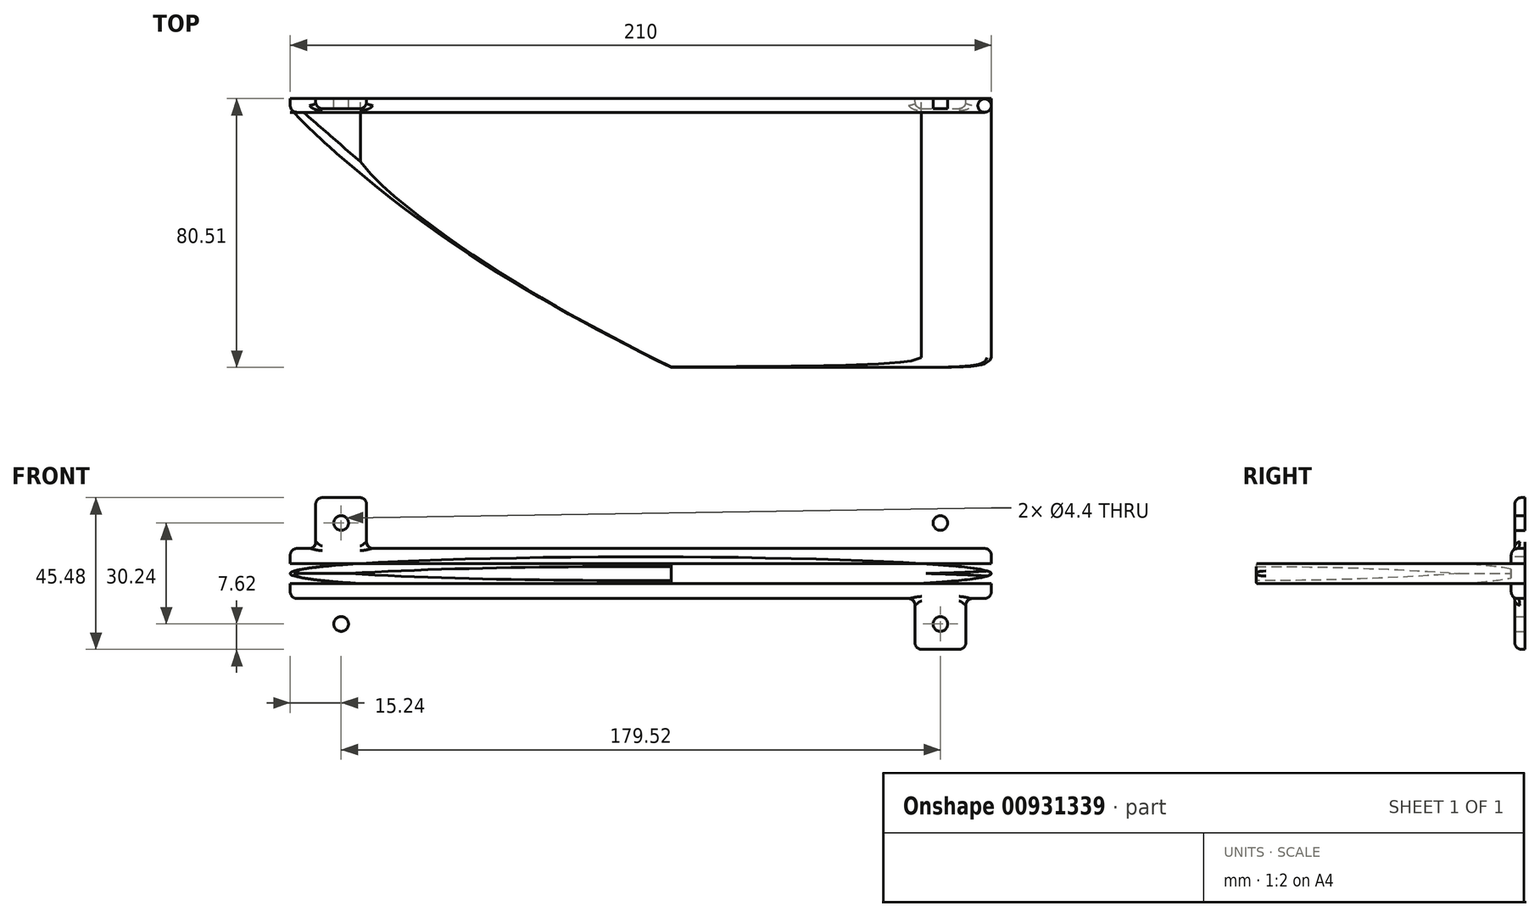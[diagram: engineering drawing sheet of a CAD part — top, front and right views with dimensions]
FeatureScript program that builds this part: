
annotation { "Feature Type Name" : "Feature", "Feature Type Description" : "" }
export const myFeature = defineFeature(function(context is Context, id is Id, definition is map)
    precondition{}
    {
        {
            var Q0;
            Q0=qCreatedBy(makeId("Top.planeOp"),FACE);
            var sketch = newSketch(context, id + "F0", { "sketchPlane" : qUnion([Q0])});
            skLineSegment(sketch, "E0", {"start": v(0, 0) * mm, "end": v(-180, 0) * mm});
            skLineSegment(sketch, "E1", {"start": v(0, 0) * mm, "end": v(30, 0) * mm});
            skLineSegment(sketch, "E2", {"start": v(30, 0) * mm, "end": v(30, -70) * mm});
            skFitSpline(sketch, "E3", {"points": [v(-180, 0) * mm, v(30, -70) * mm, v(30, 0) * mm], "startDerivative": vector(383.5, -279.58) * mm, "endDerivative": vector(-59.05, 249.16) * mm});
            skLineSegment(sketch, "E4.bottom", {"start": v(-180, 0) * mm, "end": v(50.04, 0) * mm});
            skLineSegment(sketch, "E5", {"start": v(3.9, -76.51) * mm, "end": v(3.9, 0) * mm});
            skLineSegment(sketch, "E6.bottom", {"start": v(-341.07, -177.66) * mm, "end": v(204.1, -177.66) * mm});
            skLineSegment(sketch, "E6.top", {"start": v(-341.07, 125.69) * mm, "end": v(204.1, 125.69) * mm});
            skLineSegment(sketch, "E6.left", {"start": v(-341.07, -177.66) * mm, "end": v(-341.07, 125.69) * mm});
            skLineSegment(sketch, "E6.right", {"start": v(204.1, -177.66) * mm, "end": v(204.1, 125.69) * mm});
            skPoint(sketch, "E6.middle", {"position": v(-68.48, -25.98) * mm});
            skSolve(sketch);
        }
        {
            var Q0;
            Q0=qCreatedBy(makeId("Front.planeOp"),FACE);
            var sketch = newSketch(context, id + "F1", { "sketchPlane" : qUnion([Q0])});
            skPoint(sketch, "E7", {"position": v(-75, 0) * mm});
            skLineSegment(sketch, "E8.1", {"start": v(0, 0) * mm, "end": v(30, 0) * mm});
            skEllipse(sketch, "E9", {"center": v(-75, 0) * mm, "majorRadius": 105 * mm, "minorRadius": 5 * mm, "majorAxis": v(-1, 0)});
            skLineSegment(sketch, "E10.bottom", {"start": v(-180, 3) * mm, "end": v(30, 3) * mm});
            skLineSegment(sketch, "E10.top", {"start": v(-180, -3) * mm, "end": v(30, -3) * mm});
            skLineSegment(sketch, "E10.left", {"start": v(-180, 3) * mm, "end": v(-180, -3) * mm});
            skLineSegment(sketch, "E10.right", {"start": v(30, 3) * mm, "end": v(30, -3) * mm});
            skLineSegment(sketch, "E11.bottom", {"start": v(-180, 7.5) * mm, "end": v(30, 7.5) * mm});
            skLineSegment(sketch, "E11.top", {"start": v(-180, -7.5) * mm, "end": v(30, -7.5) * mm});
            skLineSegment(sketch, "E11.left", {"start": v(-180, 7.5) * mm, "end": v(-180, -7.5) * mm});
            skLineSegment(sketch, "E11.right", {"start": v(30, 7.5) * mm, "end": v(30, -7.5) * mm});
            skSolve(sketch);
        }
        {
            var Q0;
            Q0=sQuery(id+"F0.wireOp",EDGE,"E5");
            cPlane(context, id + "F2", {"entities" : qUnion([Q0]), "cplaneType" : CPlaneType.LINE_ANGLE, "offset" : 25 * mm, "angle" : 90 * degree, "width" : 150 * mm, "height" : 150 * mm});
        }
        {
            var Q0;
            Q0=makeQuery(id+"F1.imprint","IMPRINT",FACE,{"disambiguationData":[TD([[makeQuery(id+"F1.imprint","IMPRINT",EDGE,{"derivedFrom":sQuery(id+"F1.wireOp",EDGE,"E9")}),1.0]])]});
            extrude(context, id + "F3", {"entities" : qUnion([Q0]), "depth" : 76.5 * mm, "offsetDistance" : 25 * mm});
        }
        {
            var Q0;
            Q0=qCreatedBy(makeId("Top.planeOp"),FACE);
            var sketch = newSketch(context, id + "F4", { "sketchPlane" : qUnion([Q0])});
            skFitSpline(sketch, "E12.0", {"points": [v(-180, 0) * mm, v(-98.18, -59.65) * mm, v(59.74, -108.57) * mm, v(37.08, -29.9) * mm, v(30, 0) * mm]});
            skLineSegment(sketch, "E12.1", {"start": v(30, 0) * mm, "end": v(-180, 0) * mm});
            skLineSegment(sketch, "E12.2", {"start": v(-341.07, -177.66) * mm, "end": v(-341.07, 125.69) * mm});
            skLineSegment(sketch, "E12.3", {"start": v(-341.07, -177.66) * mm, "end": v(204.1, -177.66) * mm});
            skLineSegment(sketch, "E12.4", {"start": v(-341.07, 125.69) * mm, "end": v(204.1, 125.69) * mm});
            skLineSegment(sketch, "E12.5", {"start": v(204.1, -177.66) * mm, "end": v(204.1, 125.69) * mm});
            skLineSegment(sketch, "E13", {"start": v(30, -70) * mm, "end": v(30, 0) * mm});
            skSolve(sketch);
        }
        {
            var Q0;
            Q0=makeQuery(id+"F4.imprint","IMPRINT",FACE,{"disambiguationData":[TD([[makeQuery(id+"F4.imprint","IMPRINT",EDGE,{"derivedFrom":sQuery(id+"F4.wireOp",EDGE,"E12.0")}),-1.0]])]});
            extrude(context, id + "F5", {"entities" : qUnion([Q0]), "operationType" : NewBodyOperationType.REMOVE, "endBound" : BoundingType.SYMMETRIC, "oppositeDirection" : true, "depth" : 25 * mm, "offsetDistance" : 25 * mm});
        }
        {
            var Q0;
            Q0=makeQuery(id+"F5.boolean.opBoolean","INTERSECT",EDGE,{"disambiguationData":[OD(2.0)],"derivedFrom":[makeQuery(id+"F3.opExtrude","SWEPT_FACE",FACE,{"disambiguationData":[OSD([sQuery(id+"F1.wireOp",EDGE,"E9")])]}),makeQuery(id+"F5.opExtrude","SWEPT_FACE",FACE,{"disambiguationData":[OSD([sQuery(id+"F4.wireOp",EDGE,"E12.0")])]})]});
            var Q1;
            Q1=makeQuery(id+"F5.boolean.opBoolean","INTERSECT",EDGE,{"disambiguationData":[OD(0.0)],"derivedFrom":[makeQuery(id+"F3.opExtrude","SWEPT_FACE",FACE,{"disambiguationData":[OSD([sQuery(id+"F1.wireOp",EDGE,"E9")])]}),makeQuery(id+"F5.opExtrude","SWEPT_FACE",FACE,{"disambiguationData":[OSD([sQuery(id+"F4.wireOp",EDGE,"E12.0")])]})]});
            var Q2;
            Q2=makeQuery(id+"F5.boolean.opBoolean","SPLIT",EDGE,{"disambiguationData":[OD(0.0)],"derivedFrom":makeQuery(id+"F3.opExtrude","CAP_EDGE",EDGE,{"disambiguationData":[OSD([sQuery(id+"F1.wireOp",EDGE,"E9")])],"isStart":false})});
            var Q3;
            Q3=makeQuery(id+"F5.boolean.opBoolean","INTERSECT",EDGE,{"disambiguationData":[OD(1.0)],"derivedFrom":[makeQuery(id+"F3.opExtrude","SWEPT_FACE",FACE,{"disambiguationData":[OSD([sQuery(id+"F1.wireOp",EDGE,"E9")])]}),makeQuery(id+"F5.opExtrude","SWEPT_FACE",FACE,{"disambiguationData":[OSD([sQuery(id+"F4.wireOp",EDGE,"E12.0")])]})]});
            var Q4;
            Q4=makeQuery(id+"F5.boolean.opBoolean","SPLIT",EDGE,{"disambiguationData":[OD(1.0)],"derivedFrom":makeQuery(id+"F3.opExtrude","CAP_EDGE",EDGE,{"disambiguationData":[OSD([sQuery(id+"F1.wireOp",EDGE,"E9")])],"isStart":false})});
            fillet(context, id + "F6", {"entities" : qUnion([Q0, Q1, Q2, Q3, Q4]), "radius" : 2.9 * mm, "tangentPropagation" : true, "allowEdgeOverflow" : false});
        }
        {
            var Q0;
            {var subQ0=sQuery(id+"F1.wireOp",EDGE,"E11.top");Q0=makeQuery(id+"F1.imprint","IMPRINT",FACE,{"disambiguationData":[TD([[makeQuery(id+"F1.imprint","IMPRINT",EDGE,{"derivedFrom":subQ0}),1.0]])]});}
            var Q1;
            {var subQ0=sQuery(id+"F1.wireOp",EDGE,"E10.top");var subQ1=sQuery(id+"F1.wireOp",EDGE,"E9");var subQ2=makeQuery(id+"F1.imprint","INTERSECT",VERTEX,{"disambiguationData":[OD(0.0)],"derivedFrom":[subQ1,subQ0]});Q1=makeQuery(id+"F1.imprint","IMPRINT",FACE,{"disambiguationData":[TD([[makeQuery(id+"F1.imprint","IMPRINT",EDGE,{"disambiguationData":[TD([[subQ2,-1.0]])],"derivedFrom":subQ1}),1.0]])]});}
            var Q2;
            {var subQ0=sQuery(id+"F1.wireOp",EDGE,"E10.bottom");var subQ1=sQuery(id+"F1.wireOp",EDGE,"E9");var subQ2=makeQuery(id+"F1.imprint","INTERSECT",VERTEX,{"disambiguationData":[OD(0.0)],"derivedFrom":[subQ1,subQ0]});Q2=makeQuery(id+"F1.imprint","IMPRINT",FACE,{"disambiguationData":[TD([[makeQuery(id+"F1.imprint","IMPRINT",EDGE,{"disambiguationData":[TD([[subQ2,-1.0]])],"derivedFrom":subQ1}),1.0]])]});}
            var Q3;
            {var subQ0=sQuery(id+"F1.wireOp",EDGE,"E11.bottom");Q3=makeQuery(id+"F1.imprint","IMPRINT",FACE,{"disambiguationData":[TD([[makeQuery(id+"F1.imprint","IMPRINT",EDGE,{"derivedFrom":subQ0}),-1.0]])]});}
            extrude(context, id + "F7", {"entities" : qUnion([Q0, Q1, Q2, Q3]), "operationType" : NewBodyOperationType.ADD, "depth" : 0.1 * mm, "offsetDistance" : 25 * mm});
        }
        {
            var Q0;
            {var subQ0=sQuery(id+"F1.wireOp",EDGE,"E11.bottom");Q0=makeQuery(id+"F1.imprint","IMPRINT",FACE,{"disambiguationData":[TD([[makeQuery(id+"F1.imprint","IMPRINT",EDGE,{"derivedFrom":subQ0}),-1.0]])]});}
            var Q1;
            {var subQ0=sQuery(id+"F1.wireOp",EDGE,"E10.bottom");var subQ1=sQuery(id+"F1.wireOp",EDGE,"E9");var subQ2=makeQuery(id+"F1.imprint","INTERSECT",VERTEX,{"disambiguationData":[OD(0.0)],"derivedFrom":[subQ1,subQ0]});Q1=makeQuery(id+"F1.imprint","IMPRINT",FACE,{"disambiguationData":[TD([[makeQuery(id+"F1.imprint","IMPRINT",EDGE,{"disambiguationData":[TD([[subQ2,-1.0]])],"derivedFrom":subQ1}),1.0]])]});}
            var Q2;
            {var subQ0=sQuery(id+"F1.wireOp",EDGE,"E10.top");var subQ1=sQuery(id+"F1.wireOp",EDGE,"E9");var subQ2=makeQuery(id+"F1.imprint","INTERSECT",VERTEX,{"disambiguationData":[OD(0.0)],"derivedFrom":[subQ1,subQ0]});Q2=makeQuery(id+"F1.imprint","IMPRINT",FACE,{"disambiguationData":[TD([[makeQuery(id+"F1.imprint","IMPRINT",EDGE,{"disambiguationData":[TD([[subQ2,-1.0]])],"derivedFrom":subQ1}),1.0]])]});}
            var Q3;
            {var subQ0=sQuery(id+"F1.wireOp",EDGE,"E11.top");Q3=makeQuery(id+"F1.imprint","IMPRINT",FACE,{"disambiguationData":[TD([[makeQuery(id+"F1.imprint","IMPRINT",EDGE,{"derivedFrom":subQ0}),1.0]])]});}
            extrude(context, id + "F8", {"entities" : qUnion([Q0, Q1, Q2, Q3]), "operationType" : NewBodyOperationType.ADD, "oppositeDirection" : true, "depth" : 4 * mm, "offsetDistance" : 25 * mm});
        }
        {
            var Q0;
            Q0=qCreatedBy(makeId("Front.planeOp"),FACE);
            cPlane(context, id + "F9", {"entities" : qUnion([Q0]), "cplaneType" : CPlaneType.OFFSET, "offset" : 4 * mm, "oppositeDirection" : true, "width" : 150 * mm, "height" : 150 * mm});
        }
        {
            var Q0;
            Q0=qCreatedBy(id+"F9.planeOp",FACE);
            var sketch = newSketch(context, id + "F10", { "sketchPlane" : qUnion([Q0])});
            skPoint(sketch, "E14.0", {"position": v(-75, 0) * mm});
            skLineSegment(sketch, "E15.0", {"start": v(-180, -7.5) * mm, "end": v(30, -7.5) * mm});
            skLineSegment(sketch, "E15.1", {"start": v(-180, 7.5) * mm, "end": v(30, 7.5) * mm});
            skLineSegment(sketch, "E16", {"start": v(-75, 7.5) * mm, "end": v(-75, -7.5) * mm, "construction": true});
            skLineSegment(sketch, "E17", {"start": v(-180, 0) * mm, "end": v(30, 0) * mm, "construction": true});
            skCircle(sketch, "E18", {"center": v(-164.76, 15.12) * mm, "radius": 2.2 * mm});
            skLineSegment(sketch, "E19.MirrorCS", {"start": v(-180, -7.5) * mm, "end": v(-164.76, -7.5) * mm});
            skCircle(sketch, "E20.MirrorC", {"center": v(-164.76, -15.12) * mm, "radius": 2.2 * mm});
            skCircle(sketch, "E21.MirrorC", {"center": v(14.76, 15.12) * mm, "radius": 2.2 * mm});
            skCircle(sketch, "E22.MirrorC", {"center": v(14.76, -15.12) * mm, "radius": 2.2 * mm});
            skLineSegment(sketch, "E23.bottom", {"start": v(22.38, 7.5) * mm, "end": v(7.14, 7.5) * mm});
            skLineSegment(sketch, "E23.top", {"start": v(22.38, 22.74) * mm, "end": v(7.14, 22.74) * mm});
            skLineSegment(sketch, "E23.left", {"start": v(22.38, 7.5) * mm, "end": v(22.38, 22.74) * mm});
            skLineSegment(sketch, "E23.right", {"start": v(7.14, 7.5) * mm, "end": v(7.14, 22.74) * mm});
            skLineSegment(sketch, "E24.MirrorCS", {"start": v(22.38, -7.5) * mm, "end": v(22.38, -22.74) * mm});
            skLineSegment(sketch, "E25.MirrorCS", {"start": v(22.38, -22.74) * mm, "end": v(7.14, -22.74) * mm});
            skLineSegment(sketch, "E26.MirrorCS", {"start": v(7.14, -7.5) * mm, "end": v(7.14, -22.74) * mm});
            skLineSegment(sketch, "E27.MirrorCS", {"start": v(22.38, -7.5) * mm, "end": v(7.14, -7.5) * mm});
            skLineSegment(sketch, "E28.MirrorCS", {"start": v(-172.38, -7.5) * mm, "end": v(-172.38, -22.74) * mm});
            skLineSegment(sketch, "E29.MirrorCS", {"start": v(-172.38, -22.74) * mm, "end": v(-157.14, -22.74) * mm});
            skLineSegment(sketch, "E30.MirrorCS", {"start": v(-157.14, -7.5) * mm, "end": v(-157.14, -22.74) * mm});
            skLineSegment(sketch, "E31.MirrorCS", {"start": v(-172.38, -7.5) * mm, "end": v(-157.14, -7.5) * mm});
            skLineSegment(sketch, "E32.MirrorCS", {"start": v(-172.38, 7.5) * mm, "end": v(-172.38, 22.74) * mm});
            skLineSegment(sketch, "E33.MirrorCS", {"start": v(-172.38, 22.74) * mm, "end": v(-157.14, 22.74) * mm});
            skLineSegment(sketch, "E34.MirrorCS", {"start": v(-157.14, 7.5) * mm, "end": v(-157.14, 22.74) * mm});
            skLineSegment(sketch, "E35.MirrorCS", {"start": v(-172.38, 7.5) * mm, "end": v(-157.14, 7.5) * mm});
            skSolve(sketch);
        }
        {
            var Q0;
            Q0=makeQuery(id+"F10.imprint","IMPRINT",FACE,{"disambiguationData":[TD([[makeQuery(id+"F10.imprint","IMPRINT",EDGE,{"derivedFrom":sQuery(id+"F10.wireOp",EDGE,"E22.MirrorC")}),-1.0]])]});
            var Q1;
            Q1=makeQuery(id+"F10.imprint","IMPRINT",FACE,{"disambiguationData":[TD([[makeQuery(id+"F10.imprint","IMPRINT",EDGE,{"derivedFrom":sQuery(id+"F10.wireOp",EDGE,"E21.MirrorC")}),1.0]])]});
            var Q2;
            Q2=makeQuery(id+"F10.imprint","IMPRINT",FACE,{"disambiguationData":[TD([[makeQuery(id+"F10.imprint","IMPRINT",EDGE,{"derivedFrom":sQuery(id+"F10.wireOp",EDGE,"E20.MirrorC")}),1.0]])]});
            var Q3;
            Q3=makeQuery(id+"F10.imprint","IMPRINT",FACE,{"disambiguationData":[TD([[makeQuery(id+"F10.imprint","IMPRINT",EDGE,{"derivedFrom":sQuery(id+"F10.wireOp",EDGE,"E18")}),-1.0]])]});
            extrude(context, id + "F11", {"entities" : qUnion([Q0, Q1, Q2, Q3]), "operationType" : NewBodyOperationType.ADD, "depth" : 3 * mm, "offsetDistance" : 25 * mm});
        }
        {
            var Q0;
            Q0=makeQuery(id+"F7.opExtrude","CAP_EDGE",EDGE,{"disambiguationData":[OSD([sQuery(id+"F1.wireOp",EDGE,"E11.top")])],"isStart":false});
            var Q1;
            {var subQ0=sQuery(id+"F1.wireOp",EDGE,"E11.left");Q1=makeQuery(id+"F7.opExtrude","CAP_EDGE",EDGE,{"disambiguationData":[OSD([subQ0]),TDD([makeQuery(id+"F1.imprint","IMPRINT",EDGE,{"disambiguationData":[TD([[makeQuery(id+"F1.imprint","INTERSECT",VERTEX,{"derivedFrom":[sQuery(id+"F1.wireOp",EDGE,"E10.top"),subQ0]}),-1.0]])],"derivedFrom":subQ0})])],"isStart":false});}
            var Q2;
            {var subQ0=sQuery(id+"F1.wireOp",EDGE,"E11.left");Q2=makeQuery(id+"F7.opExtrude","CAP_EDGE",EDGE,{"disambiguationData":[OSD([subQ0]),TDD([makeQuery(id+"F1.imprint","IMPRINT",EDGE,{"disambiguationData":[TD([[makeQuery(id+"F1.imprint","INTERSECT",VERTEX,{"derivedFrom":[sQuery(id+"F1.wireOp",EDGE,"E10.bottom"),subQ0]}),1.0]])],"derivedFrom":subQ0})])],"isStart":false});}
            var Q3;
            Q3=makeQuery(id+"F7.opExtrude","CAP_EDGE",EDGE,{"disambiguationData":[OSD([sQuery(id+"F1.wireOp",EDGE,"E11.bottom")])],"isStart":false});
            var Q4;
            {var subQ0=sQuery(id+"F1.wireOp",EDGE,"E11.left");var subQ1=sQuery(id+"F1.wireOp",EDGE,"E11.top");Q4=makeQuery(id+"F8.boolean.opBoolean","MERGE",EDGE,{"derivedFrom":[makeQuery(id+"F7.opExtrude","SWEPT_EDGE",EDGE,{"disambiguationData":[OSD([subQ1,subQ0])]}),makeQuery(id+"F8.opExtrude","SWEPT_EDGE",EDGE,{"disambiguationData":[OSD([subQ1,subQ0])]})]});}
            var Q5;
            {var subQ0=sQuery(id+"F1.wireOp",EDGE,"E11.left");var subQ1=sQuery(id+"F1.wireOp",EDGE,"E11.bottom");Q5=makeQuery(id+"F8.boolean.opBoolean","MERGE",EDGE,{"derivedFrom":[makeQuery(id+"F7.opExtrude","SWEPT_EDGE",EDGE,{"disambiguationData":[OSD([subQ1,subQ0])]}),makeQuery(id+"F8.opExtrude","SWEPT_EDGE",EDGE,{"disambiguationData":[OSD([subQ1,subQ0])]})]});}
            var Q6;
            {var subQ0=sQuery(id+"F1.wireOp",EDGE,"E11.right");var subQ1=sQuery(id+"F1.wireOp",EDGE,"E11.top");Q6=makeQuery(id+"F8.boolean.opBoolean","MERGE",EDGE,{"derivedFrom":[makeQuery(id+"F7.opExtrude","SWEPT_EDGE",EDGE,{"disambiguationData":[OSD([subQ1,subQ0])]}),makeQuery(id+"F8.opExtrude","SWEPT_EDGE",EDGE,{"disambiguationData":[OSD([subQ1,subQ0])]})]});}
            var Q7;
            {var subQ0=sQuery(id+"F1.wireOp",EDGE,"E11.right");Q7=makeQuery(id+"F7.opExtrude","CAP_EDGE",EDGE,{"disambiguationData":[OSD([subQ0]),TDD([makeQuery(id+"F1.imprint","IMPRINT",EDGE,{"disambiguationData":[TD([[makeQuery(id+"F1.imprint","INTERSECT",VERTEX,{"derivedFrom":[sQuery(id+"F1.wireOp",EDGE,"E10.top"),subQ0]}),-1.0]])],"derivedFrom":subQ0})])],"isStart":false});}
            var Q8;
            {var subQ0=sQuery(id+"F1.wireOp",EDGE,"E11.right");Q8=makeQuery(id+"F7.opExtrude","CAP_EDGE",EDGE,{"disambiguationData":[OSD([subQ0]),TDD([makeQuery(id+"F1.imprint","IMPRINT",EDGE,{"disambiguationData":[TD([[makeQuery(id+"F1.imprint","INTERSECT",VERTEX,{"derivedFrom":[sQuery(id+"F1.wireOp",EDGE,"E10.bottom"),subQ0]}),1.0]])],"derivedFrom":subQ0})])],"isStart":false});}
            var Q9;
            {var subQ0=sQuery(id+"F1.wireOp",EDGE,"E11.right");var subQ1=sQuery(id+"F1.wireOp",EDGE,"E11.bottom");Q9=makeQuery(id+"F8.boolean.opBoolean","MERGE",EDGE,{"derivedFrom":[makeQuery(id+"F7.opExtrude","SWEPT_EDGE",EDGE,{"disambiguationData":[OSD([subQ1,subQ0])]}),makeQuery(id+"F8.opExtrude","SWEPT_EDGE",EDGE,{"disambiguationData":[OSD([subQ1,subQ0])]})]});}
            fillet(context, id + "F12", {"entities" : qUnion([Q0, Q1, Q2, Q3, Q4, Q5, Q6, Q7, Q8, Q9]), "radius" : 2 * mm, "tangentPropagation" : true, "allowEdgeOverflow" : false});
        }
        {
            var Q0;
            Q0=makeQuery(id+"F11.opExtrude","CAP_EDGE",EDGE,{"disambiguationData":[OSD([sQuery(id+"F10.wireOp",EDGE,"E28.MirrorCS")])],"isStart":false});
            var Q1;
            Q1=makeQuery(id+"F11.opExtrude","CAP_EDGE",EDGE,{"disambiguationData":[OSD([sQuery(id+"F10.wireOp",EDGE,"E30.MirrorCS")])],"isStart":false});
            var Q2;
            Q2=makeQuery(id+"F11.opExtrude","CAP_EDGE",EDGE,{"disambiguationData":[OSD([sQuery(id+"F10.wireOp",EDGE,"E29.MirrorCS")])],"isStart":false});
            var Q3;
            Q3=makeQuery(id+"F11.opExtrude","SWEPT_EDGE",EDGE,{"disambiguationData":[OSD([sQuery(id+"F10.wireOp",EDGE,"E28.MirrorCS"),sQuery(id+"F10.wireOp",EDGE,"E29.MirrorCS")])]});
            var Q4;
            Q4=makeQuery(id+"F11.opExtrude","SWEPT_EDGE",EDGE,{"disambiguationData":[OSD([sQuery(id+"F10.wireOp",EDGE,"E29.MirrorCS"),sQuery(id+"F10.wireOp",EDGE,"E30.MirrorCS")])]});
            var Q5;
            Q5=makeQuery(id+"F11.opExtrude","SWEPT_EDGE",EDGE,{"disambiguationData":[OSD([sQuery(id+"F10.wireOp",EDGE,"E33.MirrorCS"),sQuery(id+"F10.wireOp",EDGE,"E34.MirrorCS")])]});
            var Q6;
            Q6=makeQuery(id+"F11.opExtrude","CAP_EDGE",EDGE,{"disambiguationData":[OSD([sQuery(id+"F10.wireOp",EDGE,"E34.MirrorCS")])],"isStart":false});
            var Q7;
            Q7=makeQuery(id+"F11.opExtrude","CAP_EDGE",EDGE,{"disambiguationData":[OSD([sQuery(id+"F10.wireOp",EDGE,"E33.MirrorCS")])],"isStart":false});
            var Q8;
            Q8=makeQuery(id+"F11.opExtrude","CAP_EDGE",EDGE,{"disambiguationData":[OSD([sQuery(id+"F10.wireOp",EDGE,"E32.MirrorCS")])],"isStart":false});
            var Q9;
            Q9=makeQuery(id+"F11.opExtrude","SWEPT_EDGE",EDGE,{"disambiguationData":[OSD([sQuery(id+"F10.wireOp",EDGE,"E32.MirrorCS"),sQuery(id+"F10.wireOp",EDGE,"E33.MirrorCS")])]});
            var Q10;
            Q10=makeQuery(id+"F11.opExtrude","SWEPT_EDGE",EDGE,{"disambiguationData":[OSD([sQuery(id+"F10.wireOp",EDGE,"E23.top"),sQuery(id+"F10.wireOp",EDGE,"E23.left")])]});
            var Q11;
            Q11=makeQuery(id+"F11.opExtrude","CAP_EDGE",EDGE,{"disambiguationData":[OSD([sQuery(id+"F10.wireOp",EDGE,"E23.left")])],"isStart":false});
            var Q12;
            Q12=makeQuery(id+"F11.opExtrude","CAP_EDGE",EDGE,{"disambiguationData":[OSD([sQuery(id+"F10.wireOp",EDGE,"E23.top")])],"isStart":false});
            var Q13;
            Q13=makeQuery(id+"F11.opExtrude","SWEPT_EDGE",EDGE,{"disambiguationData":[OSD([sQuery(id+"F10.wireOp",EDGE,"E23.top"),sQuery(id+"F10.wireOp",EDGE,"E23.right")])]});
            var Q14;
            Q14=makeQuery(id+"F11.opExtrude","CAP_EDGE",EDGE,{"disambiguationData":[OSD([sQuery(id+"F10.wireOp",EDGE,"E23.right")])],"isStart":false});
            var Q15;
            Q15=makeQuery(id+"F11.opExtrude","SWEPT_EDGE",EDGE,{"disambiguationData":[OSD([sQuery(id+"F10.wireOp",EDGE,"E24.MirrorCS"),sQuery(id+"F10.wireOp",EDGE,"E25.MirrorCS")])]});
            var Q16;
            Q16=makeQuery(id+"F11.opExtrude","SWEPT_EDGE",EDGE,{"disambiguationData":[OSD([sQuery(id+"F10.wireOp",EDGE,"E25.MirrorCS"),sQuery(id+"F10.wireOp",EDGE,"E26.MirrorCS")])]});
            var Q17;
            Q17=makeQuery(id+"F11.opExtrude","CAP_EDGE",EDGE,{"disambiguationData":[OSD([sQuery(id+"F10.wireOp",EDGE,"E26.MirrorCS")])],"isStart":false});
            var Q18;
            Q18=makeQuery(id+"F11.opExtrude","CAP_EDGE",EDGE,{"disambiguationData":[OSD([sQuery(id+"F10.wireOp",EDGE,"E25.MirrorCS")])],"isStart":false});
            var Q19;
            Q19=makeQuery(id+"F11.opExtrude","CAP_EDGE",EDGE,{"disambiguationData":[OSD([sQuery(id+"F10.wireOp",EDGE,"E24.MirrorCS")])],"isStart":false});
            fillet(context, id + "F13", {"entities" : qUnion([Q0, Q1, Q2, Q3, Q4, Q5, Q6, Q7, Q8, Q9, Q10, Q11, Q12, Q13, Q14, Q15, Q16, Q17, Q18, Q19]), "radius" : 2 * mm, "tangentPropagation" : true, "allowEdgeOverflow" : false});
        }
        {
            var Q0;
            Q0=makeQuery(id+"F12.opFillet","BLEND_EDGE",EDGE,{"blendedFrom":[makeQuery(id+"F7.opExtrude","CAP_EDGE",EDGE,{"disambiguationData":[OSD([sQuery(id+"F1.wireOp",EDGE,"E11.top")])],"isStart":false}),makeQuery(id+"F11.opExtrude","CAP_FACE",FACE,{"disambiguationData":[OSD([sQuery(id+"F10.wireOp",EDGE,"E22.MirrorC"),sQuery(id+"F10.wireOp",EDGE,"E24.MirrorCS"),sQuery(id+"F10.wireOp",EDGE,"E25.MirrorCS"),sQuery(id+"F10.wireOp",EDGE,"E26.MirrorCS"),sQuery(id+"F10.wireOp",EDGE,"E27.MirrorCS")])],"isStart":false})],"blendedInto":[makeQuery(id+"F11.opExtrude","CAP_FACE",FACE,{"disambiguationData":[OSD([sQuery(id+"F10.wireOp",EDGE,"E22.MirrorC"),sQuery(id+"F10.wireOp",EDGE,"E24.MirrorCS"),sQuery(id+"F10.wireOp",EDGE,"E25.MirrorCS"),sQuery(id+"F10.wireOp",EDGE,"E26.MirrorCS"),sQuery(id+"F10.wireOp",EDGE,"E27.MirrorCS")])],"isStart":false})]});
            var Q1;
            Q1=makeQuery(id+"F12.opFillet","BLEND_EDGE",EDGE,{"blendedFrom":[makeQuery(id+"F7.opExtrude","CAP_EDGE",EDGE,{"disambiguationData":[OSD([sQuery(id+"F1.wireOp",EDGE,"E11.bottom")])],"isStart":false}),makeQuery(id+"F11.opExtrude","CAP_FACE",FACE,{"disambiguationData":[OSD([sQuery(id+"F10.wireOp",EDGE,"E21.MirrorC"),sQuery(id+"F10.wireOp",EDGE,"E23.bottom"),sQuery(id+"F10.wireOp",EDGE,"E23.top"),sQuery(id+"F10.wireOp",EDGE,"E23.left"),sQuery(id+"F10.wireOp",EDGE,"E23.right")])],"isStart":false})],"blendedInto":[makeQuery(id+"F11.opExtrude","CAP_FACE",FACE,{"disambiguationData":[OSD([sQuery(id+"F10.wireOp",EDGE,"E21.MirrorC"),sQuery(id+"F10.wireOp",EDGE,"E23.bottom"),sQuery(id+"F10.wireOp",EDGE,"E23.top"),sQuery(id+"F10.wireOp",EDGE,"E23.left"),sQuery(id+"F10.wireOp",EDGE,"E23.right")])],"isStart":false})]});
            var Q2;
            Q2=makeQuery(id+"F12.opFillet","BLEND_EDGE",EDGE,{"blendedFrom":[makeQuery(id+"F7.opExtrude","CAP_EDGE",EDGE,{"disambiguationData":[OSD([sQuery(id+"F1.wireOp",EDGE,"E11.bottom")])],"isStart":false}),makeQuery(id+"F11.opExtrude","CAP_FACE",FACE,{"disambiguationData":[OSD([sQuery(id+"F10.wireOp",EDGE,"E18"),sQuery(id+"F10.wireOp",EDGE,"E32.MirrorCS"),sQuery(id+"F10.wireOp",EDGE,"E33.MirrorCS"),sQuery(id+"F10.wireOp",EDGE,"E34.MirrorCS"),sQuery(id+"F10.wireOp",EDGE,"E35.MirrorCS")])],"isStart":false})],"blendedInto":[makeQuery(id+"F11.opExtrude","CAP_FACE",FACE,{"disambiguationData":[OSD([sQuery(id+"F10.wireOp",EDGE,"E18"),sQuery(id+"F10.wireOp",EDGE,"E32.MirrorCS"),sQuery(id+"F10.wireOp",EDGE,"E33.MirrorCS"),sQuery(id+"F10.wireOp",EDGE,"E34.MirrorCS"),sQuery(id+"F10.wireOp",EDGE,"E35.MirrorCS")])],"isStart":false})]});
            var Q3;
            Q3=makeQuery(id+"F12.opFillet","BLEND_EDGE",EDGE,{"blendedFrom":[makeQuery(id+"F7.opExtrude","CAP_EDGE",EDGE,{"disambiguationData":[OSD([sQuery(id+"F1.wireOp",EDGE,"E11.top")])],"isStart":false}),makeQuery(id+"F11.opExtrude","CAP_FACE",FACE,{"disambiguationData":[OSD([sQuery(id+"F10.wireOp",EDGE,"E20.MirrorC"),sQuery(id+"F10.wireOp",EDGE,"E28.MirrorCS"),sQuery(id+"F10.wireOp",EDGE,"E29.MirrorCS"),sQuery(id+"F10.wireOp",EDGE,"E30.MirrorCS"),sQuery(id+"F10.wireOp",EDGE,"E31.MirrorCS")])],"isStart":false})],"blendedInto":[makeQuery(id+"F11.opExtrude","CAP_FACE",FACE,{"disambiguationData":[OSD([sQuery(id+"F10.wireOp",EDGE,"E20.MirrorC"),sQuery(id+"F10.wireOp",EDGE,"E28.MirrorCS"),sQuery(id+"F10.wireOp",EDGE,"E29.MirrorCS"),sQuery(id+"F10.wireOp",EDGE,"E30.MirrorCS"),sQuery(id+"F10.wireOp",EDGE,"E31.MirrorCS")])],"isStart":false})]});
            fillet(context, id + "F14", {"entities" : qUnion([Q0, Q1, Q2, Q3]), "radius" : 2 * mm, "tangentPropagation" : true, "allowEdgeOverflow" : false});
        }
    });
